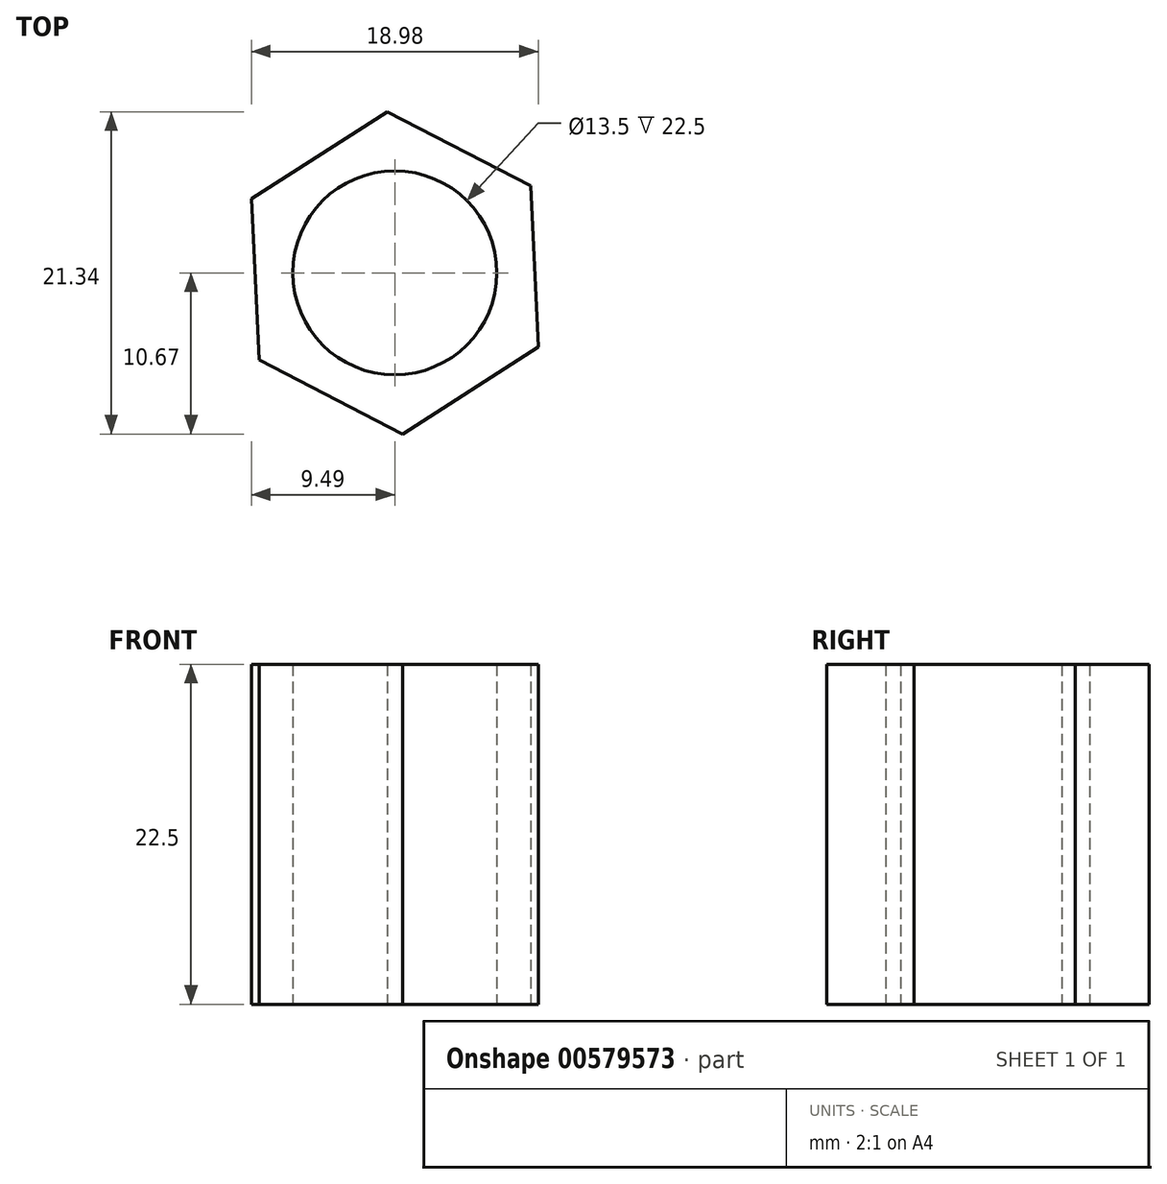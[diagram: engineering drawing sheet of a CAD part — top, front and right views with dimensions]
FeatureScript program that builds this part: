
annotation { "Feature Type Name" : "Feature", "Feature Type Description" : "" }
export const myFeature = defineFeature(function(context is Context, id is Id, definition is map)
    precondition{}
    {
        {
            var Q0;
            Q0=qCreatedBy(makeId("Top.planeOp"),FACE);
            var sketch = newSketch(context, id + "F0", { "sketchPlane" : qUnion([Q0])});
            skCircle(sketch, "E0.cCircle", {"center": v(0, 0) * mm, "radius": 9.25 * mm, "construction": true});
            skLineSegment(sketch, "E0.0", {"start": v(-9.5, 4.9) * mm, "end": v(-0.5, 10.67) * mm});
            skLineSegment(sketch, "E0.1", {"start": v(-0.5, 10.67) * mm, "end": v(8.99, 5.77) * mm});
            skLineSegment(sketch, "E0.2", {"start": v(8.99, 5.77) * mm, "end": v(9.5, -4.9) * mm});
            skLineSegment(sketch, "E0.3", {"start": v(9.5, -4.9) * mm, "end": v(0.5, -10.67) * mm});
            skLineSegment(sketch, "E0.4", {"start": v(0.5, -10.67) * mm, "end": v(-8.99, -5.77) * mm});
            skLineSegment(sketch, "E0.5", {"start": v(-8.99, -5.77) * mm, "end": v(-9.5, 4.9) * mm});
            skPoint(sketch, "E0.0.midPoint", {"position": v(-5, 7.78) * mm});
            skSolve(sketch);
        }
        {
            var Q0;
            Q0=qCreatedBy(makeId("Top.planeOp"),FACE);
            var sketch = newSketch(context, id + "F1", { "sketchPlane" : qUnion([Q0])});
            skCircle(sketch, "E1", {"center": v(0, 0) * mm, "radius": 12.7 * mm});
            skSolve(sketch);
        }
        {
            var Q0;
            Q0=makeQuery(id+"F0.imprint","IMPRINT",FACE,{"disambiguationData":[TD([[makeQuery(id+"F0.imprint","IMPRINT",EDGE,{"derivedFrom":sQuery(id+"F0.wireOp",EDGE,"E0.0")}),-1.0]])]});
            extrude(context, id + "F2", {"entities" : qUnion([Q0]), "depth" : 22.5 * mm, "offsetDistance" : 25 * mm});
        }
        {
            var Q0;
            Q0=makeQuery(id+"F1.imprint","IMPRINT",FACE,{"disambiguationData":[TD([[makeQuery(id+"F1.imprint","IMPRINT",EDGE,{"derivedFrom":sQuery(id+"F1.wireOp",EDGE,"E1")}),1.0]])]});
            var sketch = newSketch(context, id + "F3", { "sketchPlane" : qUnion([Q0])});
            skCircle(sketch, "E2", {"center": v(0, 0) * mm, "radius": 6.75 * mm});
            skSolve(sketch);
        }
        {
            var Q0;
            Q0=makeQuery(id+"F3.imprint","IMPRINT",FACE,{"disambiguationData":[TD([[makeQuery(id+"F3.imprint","IMPRINT",EDGE,{"derivedFrom":sQuery(id+"F3.wireOp",EDGE,"E2")}),1.0]])]});
            extrude(context, id + "F4", {"entities" : qUnion([Q0]), "operationType" : NewBodyOperationType.REMOVE, "depth" : 25 * mm, "offsetDistance" : 25 * mm});
        }
    });
